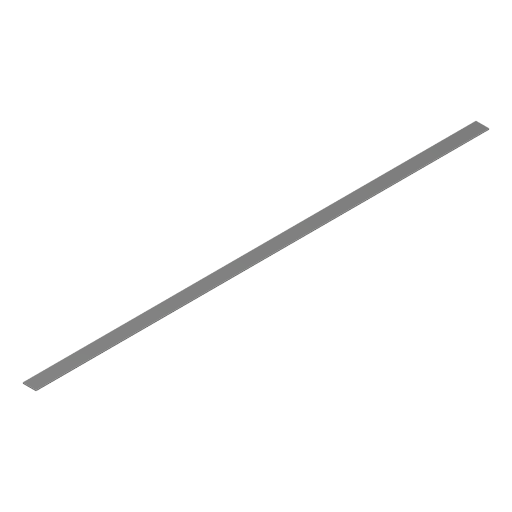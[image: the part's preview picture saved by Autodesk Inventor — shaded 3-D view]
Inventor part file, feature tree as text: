
AUTODESK INVENTOR PART (.ipt)
format: ipt  version: 2024.3 (Build 283343000, 343)  size: 84,480 bytes
history: native  units: mm
features: extrude x1, sketch x1
ambient origin geometry x8: Origin, YZ Plane, XZ Plane, XY Plane, X Axis, Y Axis, Z Axis, Center Point
bodies: Solid1 (feature_tree)
feature tree (2):
  extrude  "Extrusion1"  Depth=680.0mm
  sketch  "Sketch1"  dims[d0=20.0mm d1=680.0mm d2=1.4mm d3=0.0mm]
